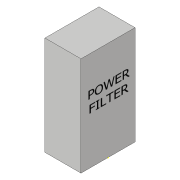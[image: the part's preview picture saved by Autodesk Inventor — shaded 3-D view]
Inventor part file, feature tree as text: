
AUTODESK INVENTOR PART (.ipt)
format: ipt  version: 2017 (Build 210142000, 142)  size: 81,920 bytes
history: native  units: in
note: dims shown in document units (in); Inventor stores cm internally (conversion verified against a paired STEP export)
features: sketch x2, other x1, extrude x1, hole x1
ambient origin geometry x8: Origin, YZ Plane, XZ Plane, XY Plane, X Axis, Y Axis, Z Axis, Center Point
bodies: Solid1 (feature_tree)
feature tree (5):
  other  "RFI_power_filter"
  extrude  "Extrusion1"  Depth=7.0866in
  sketch  "Sketch2"  dims[d2=4.7244in d3=0.0in d4=1.9685in d5=3.5433in d6=1.0in d7=0.75in d8=0.375in d9=0.25in d10=0.5635in d11=1.0in d12=0.0in]
  hole  "Hole1"  [1 undecoded]
  sketch  "Sketch1"  dims[d0=12.9921in d1=7.0866in]
note: 1 required parameter value undecoded (feature->parameter linkage not recoverable at this tier; creation-order binding heuristic only, values carry confidence <= 0.55)
